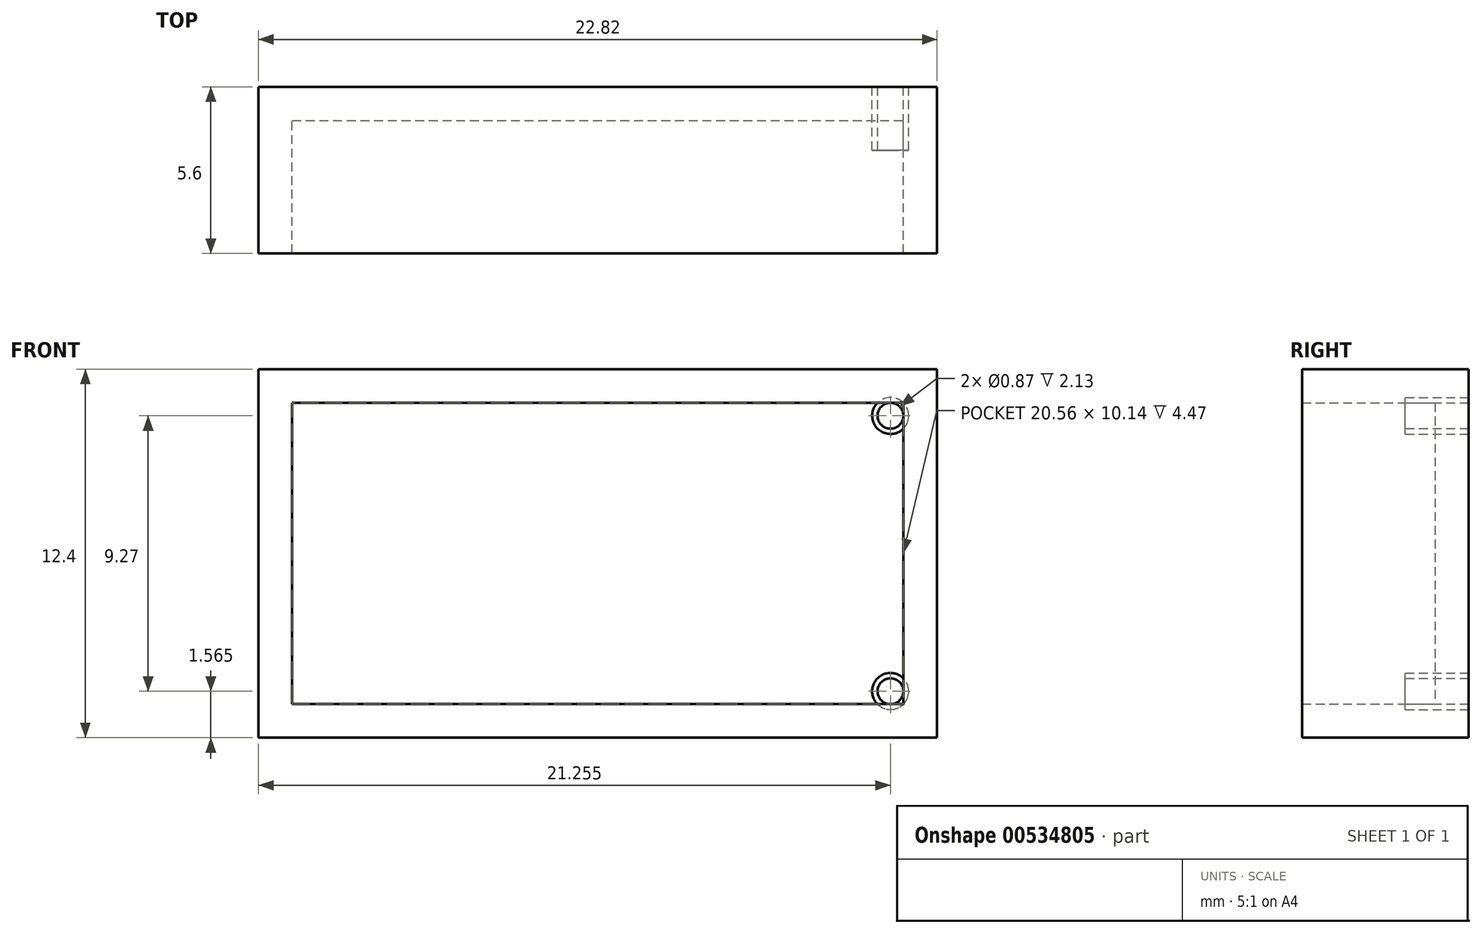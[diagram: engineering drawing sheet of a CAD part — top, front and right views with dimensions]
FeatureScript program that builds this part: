
annotation { "Feature Type Name" : "Feature", "Feature Type Description" : "" }
export const myFeature = defineFeature(function(context is Context, id is Id, definition is map)
    precondition{}
    {
        {
            var Q0;
            Q0=qCreatedBy(makeId("Front.planeOp"),FACE);
            var sketch = newSketch(context, id + "F0", { "sketchPlane" : qUnion([Q0])});
            skLineSegment(sketch, "E0.bottom", {"start": v(-11.41, 6.2) * mm, "end": v(11.4, 6.2) * mm});
            skLineSegment(sketch, "E0.top", {"start": v(-11.41, -6.2) * mm, "end": v(11.4, -6.2) * mm});
            skLineSegment(sketch, "E0.left", {"start": v(-11.4, 6.2) * mm, "end": v(-11.41, -6.2) * mm});
            skLineSegment(sketch, "E0.right", {"start": v(11.4, 6.2) * mm, "end": v(11.4, -6.2) * mm});
            skPoint(sketch, "E0.middle", {"position": v(0, 0) * mm});
            skSolve(sketch);
        }
        {
            var Q0;
            Q0=makeQuery(id+"F0.imprint","IMPRINT",FACE,{"disambiguationData":[TD([[makeQuery(id+"F0.imprint","IMPRINT",EDGE,{"derivedFrom":sQuery(id+"F0.wireOp",EDGE,"E0.bottom")}),-1.0]])]});
            extrude(context, id + "F1", {"entities" : qUnion([Q0]), "depth" : 5.6 * mm, "offsetDistance" : 25 * mm});
        }
        {
            var Q0;
            Q0=makeQuery(id+"F1.opExtrude","CAP_FACE",FACE,{"disambiguationData":[OSD([sQuery(id+"F0.wireOp",EDGE,"E0.bottom"),sQuery(id+"F0.wireOp",EDGE,"E0.top"),sQuery(id+"F0.wireOp",EDGE,"E0.left"),sQuery(id+"F0.wireOp",EDGE,"E0.right")])],"isStart":false});
            shell(context, id + "F2", {"entities" : qUnion([Q0]), "thickness" : 1.13 * mm});
        }
        {
            var Q0;
            Q0=qCreatedBy(makeId("Front.planeOp"),FACE);
            var sketch = newSketch(context, id + "F3", { "sketchPlane" : qUnion([Q0])});
            skCircle(sketch, "E1", {"center": v(9.84, 4.64) * mm, "radius": 0.43 * mm});
            skCircle(sketch, "E2", {"center": v(9.84, 4.64) * mm, "radius": 0.61 * mm});
            skPoint(sketch, "E3", {"position": v(9.84, 5.07) * mm});
            skPoint(sketch, "E4", {"position": v(9.4, 4.64) * mm});
            skPoint(sketch, "E5", {"position": v(9.84, 4.2) * mm});
            skPoint(sketch, "E6", {"position": v(10.28, 4.64) * mm});
            skSolve(sketch);
        }
        {
            var Q0;
            Q0=qCreatedBy(makeId("Front.planeOp"),FACE);
            var sketch = newSketch(context, id + "F4", { "sketchPlane" : qUnion([Q0])});
            skCircle(sketch, "E7", {"center": v(9.84, -4.63) * mm, "radius": 0.43 * mm});
            skCircle(sketch, "E8", {"center": v(9.84, -4.63) * mm, "radius": 0.61 * mm});
            skPoint(sketch, "E9", {"position": v(9.84, -4.2) * mm});
            skPoint(sketch, "E10", {"position": v(9.4, -4.63) * mm});
            skPoint(sketch, "E11", {"position": v(9.84, -5.07) * mm});
            skPoint(sketch, "E12", {"position": v(10.28, -4.63) * mm});
            skSolve(sketch);
        }
        {
            var Q0;
            Q0=makeQuery(id+"F3.imprint","IMPRINT",FACE,{"disambiguationData":[TD([[makeQuery(id+"F3.imprint","IMPRINT",EDGE,{"derivedFrom":sQuery(id+"F3.wireOp",EDGE,"E1")}),-1.0]])]});
            extrude(context, id + "F5", {"entities" : qUnion([Q0]), "depth" : 2.13 * mm, "offsetDistance" : 25 * mm});
        }
        {
            var Q0;
            Q0=makeQuery(id+"F4.imprint","IMPRINT",FACE,{"disambiguationData":[TD([[makeQuery(id+"F4.imprint","IMPRINT",EDGE,{"derivedFrom":sQuery(id+"F4.wireOp",EDGE,"E7")}),-1.0]])]});
            extrude(context, id + "F6", {"entities" : qUnion([Q0]), "depth" : 2.13 * mm, "offsetDistance" : 25 * mm});
        }
    });
